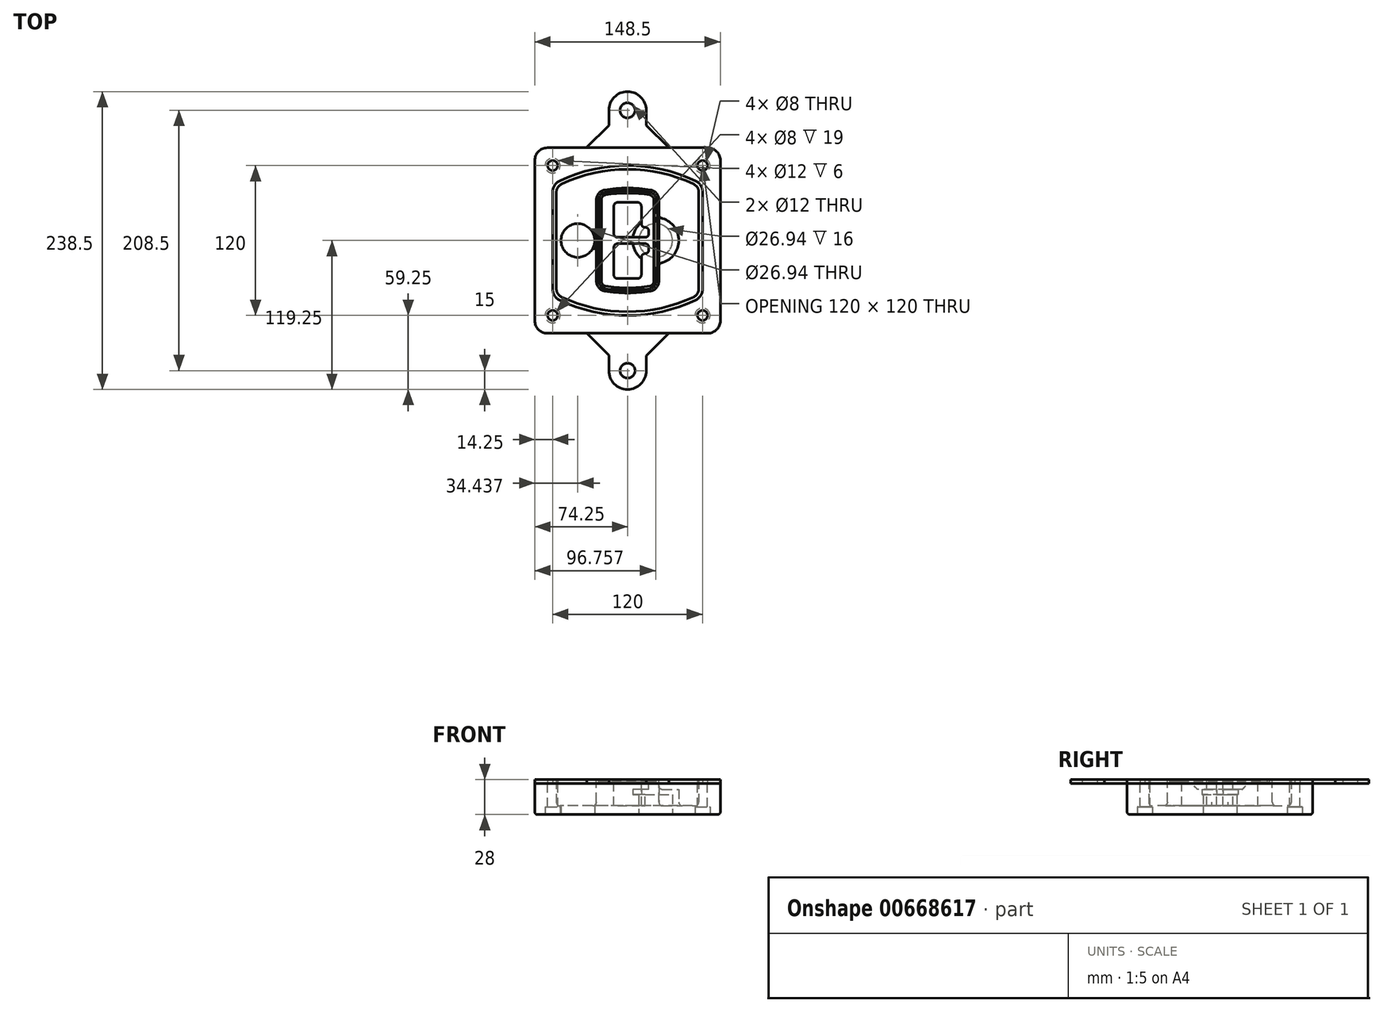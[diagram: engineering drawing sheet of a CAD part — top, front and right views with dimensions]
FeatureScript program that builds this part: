
annotation { "Feature Type Name" : "Feature", "Feature Type Description" : "" }
export const myFeature = defineFeature(function(context is Context, id is Id, definition is map)
    precondition{}
    {
        {
            var Q0;
            Q0=qCreatedBy(makeId("Top.planeOp"),FACE);
            var sketch = newSketch(context, id + "F0", { "sketchPlane" : qUnion([Q0])});
            skPoint(sketch, "E0.rect.middle", {"position": v(0, 0) * mm});
            skLineSegment(sketch, "E1.bottom", {"start": v(-64.25, -74.25) * mm, "end": v(64.25, -74.25) * mm});
            skLineSegment(sketch, "E1.top", {"start": v(-64.25, 74.25) * mm, "end": v(64.25, 74.25) * mm});
            skLineSegment(sketch, "E1.left", {"start": v(-74.25, -64.25) * mm, "end": v(-74.25, 64.25) * mm});
            skLineSegment(sketch, "E1.right", {"start": v(74.25, -64.25) * mm, "end": v(74.25, 64.25) * mm});
            skLineSegment(sketch, "E2", {"start": v(-74.25, 74.25) * mm, "end": v(74.25, -74.25) * mm, "construction": true});
            skLineSegment(sketch, "E3", {"start": v(74.25, 74.25) * mm, "end": v(-74.25, -74.25) * mm, "construction": true});
            skCircle(sketch, "E4", {"center": v(-60, 60) * mm, "radius": 4 * mm});
            skCircle(sketch, "E5", {"center": v(60, 60) * mm, "radius": 4 * mm});
            skCircle(sketch, "E6", {"center": v(60, -60) * mm, "radius": 4 * mm});
            skCircle(sketch, "E7", {"center": v(-60, -60) * mm, "radius": 4 * mm});
            skLineSegment(sketch, "E8", {"start": v(-60, 60) * mm, "end": v(60, 60) * mm, "construction": true});
            skLineSegment(sketch, "E9", {"start": v(60, 60) * mm, "end": v(60, -60) * mm, "construction": true});
            skLineSegment(sketch, "E10", {"start": v(60, -60) * mm, "end": v(-60, -60) * mm, "construction": true});
            skLineSegment(sketch, "E11", {"start": v(-60, -60) * mm, "end": v(-60, 60) * mm, "construction": true});
            skLineSegment(sketch, "E12", {"start": v(-60, 38.83) * mm, "end": v(-60, -38.83) * mm});
            skLineSegment(sketch, "E13", {"start": v(60, 38.83) * mm, "end": v(60, -38.83) * mm});
            skArc(sketch, "E14", {"start": v(54.26, 47.88) * mm, "mid": v(0, 60) * mm, "end": v(-54.26, 47.88) * mm});
            skArc(sketch, "E15", {"start": v(-54.26, -47.88) * mm, "mid": v(0, -60) * mm, "end": v(54.26, -47.88) * mm});
            skLineSegment(sketch, "E16", {"start": v(-60, 0) * mm, "end": v(60, 0) * mm, "construction": true});
            skPoint(sketch, "E17.visualSharp", {"position": v(-60, -45) * mm});
            skArc(sketch, "E17.filletArc", {"start": v(-60, -38.83) * mm, "mid": v(-58.44, -44.2) * mm, "end": v(-54.26, -47.88) * mm});
            skPoint(sketch, "E18.visualSharp", {"position": v(-60, 45) * mm});
            skArc(sketch, "E18.filletArc", {"start": v(-54.26, 47.88) * mm, "mid": v(-58.44, 44.2) * mm, "end": v(-60, 38.83) * mm});
            skPoint(sketch, "E19.visualSharp", {"position": v(60, 45) * mm});
            skArc(sketch, "E19.filletArc", {"start": v(60, 38.83) * mm, "mid": v(58.44, 44.2) * mm, "end": v(54.26, 47.88) * mm});
            skPoint(sketch, "E20.visualSharp", {"position": v(60, -45) * mm});
            skArc(sketch, "E20.filletArc", {"start": v(54.26, -47.88) * mm, "mid": v(58.44, -44.2) * mm, "end": v(60, -38.83) * mm});
            skPoint(sketch, "E21.visualSharp", {"position": v(-74.25, 74.25) * mm});
            skArc(sketch, "E21.filletArc", {"start": v(-64.25, 74.25) * mm, "mid": v(-71.32, 71.32) * mm, "end": v(-74.25, 64.25) * mm});
            skPoint(sketch, "E22.visualSharp", {"position": v(74.25, 74.25) * mm});
            skArc(sketch, "E22.filletArc", {"start": v(74.25, 64.25) * mm, "mid": v(71.32, 71.32) * mm, "end": v(64.25, 74.25) * mm});
            skPoint(sketch, "E23.visualSharp", {"position": v(74.25, -74.25) * mm});
            skArc(sketch, "E23.filletArc", {"start": v(64.25, -74.25) * mm, "mid": v(71.32, -71.32) * mm, "end": v(74.25, -64.25) * mm});
            skPoint(sketch, "E24.visualSharp", {"position": v(-74.25, -74.25) * mm});
            skArc(sketch, "E24.filletArc", {"start": v(-74.25, -64.25) * mm, "mid": v(-71.32, -71.32) * mm, "end": v(-64.25, -74.25) * mm});
            skArc(sketch, "E25.0", {"start": v(57, 38.83) * mm, "mid": v(55.9, 42.58) * mm, "end": v(52.98, 45.17) * mm});
            skLineSegment(sketch, "E25.1", {"start": v(57, 38.83) * mm, "end": v(57, -38.83) * mm});
            skArc(sketch, "E25.2", {"start": v(52.98, -45.17) * mm, "mid": v(55.9, -42.58) * mm, "end": v(57, -38.83) * mm});
            skArc(sketch, "E25.3", {"start": v(-52.98, -45.17) * mm, "mid": v(0, -57) * mm, "end": v(52.98, -45.17) * mm});
            skArc(sketch, "E25.4", {"start": v(-57, -38.83) * mm, "mid": v(-55.9, -42.58) * mm, "end": v(-52.98, -45.17) * mm});
            skArc(sketch, "E25.5", {"start": v(52.98, 45.17) * mm, "mid": v(0, 57) * mm, "end": v(-52.98, 45.17) * mm});
            skLineSegment(sketch, "E25.6", {"start": v(-57, 38.83) * mm, "end": v(-57, -38.83) * mm});
            skArc(sketch, "E25.7", {"start": v(-52.98, 45.17) * mm, "mid": v(-55.9, 42.58) * mm, "end": v(-57, 38.83) * mm});
            skArc(sketch, "E26.0", {"start": v(-55.96, 51.5) * mm, "mid": v(-61.82, 46.33) * mm, "end": v(-64, 38.83) * mm});
            skArc(sketch, "E26.1", {"start": v(55.96, 51.5) * mm, "mid": v(0, 64) * mm, "end": v(-55.96, 51.5) * mm});
            skArc(sketch, "E26.2", {"start": v(64, 38.83) * mm, "mid": v(61.82, 46.33) * mm, "end": v(55.96, 51.5) * mm});
            skLineSegment(sketch, "E26.3", {"start": v(64, 38.83) * mm, "end": v(64, -38.83) * mm});
            skArc(sketch, "E26.4", {"start": v(55.96, -51.5) * mm, "mid": v(61.82, -46.33) * mm, "end": v(64, -38.83) * mm});
            skLineSegment(sketch, "E26.5", {"start": v(-64, 38.83) * mm, "end": v(-64, -38.83) * mm});
            skArc(sketch, "E26.6", {"start": v(-55.96, -51.5) * mm, "mid": v(0, -64) * mm, "end": v(55.96, -51.5) * mm});
            skArc(sketch, "E26.7", {"start": v(-64, -38.83) * mm, "mid": v(-61.82, -46.33) * mm, "end": v(-55.96, -51.5) * mm});
            skSolve(sketch);
        }
        {
            var Q0;
            Q0=makeQuery(id+"F0.imprint","IMPRINT",FACE,{"disambiguationData":[TD([[makeQuery(id+"F0.imprint","IMPRINT",EDGE,{"derivedFrom":sQuery(id+"F0.wireOp",EDGE,"E1.bottom")}),1.0]])]});
            var Q1;
            Q1=makeQuery(id+"F0.imprint","IMPRINT",FACE,{"disambiguationData":[TD([[makeQuery(id+"F0.imprint","IMPRINT",EDGE,{"derivedFrom":sQuery(id+"F0.wireOp",EDGE,"E12")}),1.0]])]});
            var Q2;
            Q2=makeQuery(id+"F0.imprint","IMPRINT",FACE,{"disambiguationData":[TD([[makeQuery(id+"F0.imprint","IMPRINT",EDGE,{"derivedFrom":sQuery(id+"F0.wireOp",EDGE,"E25.0")}),1.0]])]});
            var Q3;
            Q3=makeQuery(id+"F0.imprint","IMPRINT",FACE,{"disambiguationData":[TD([[makeQuery(id+"F0.imprint","IMPRINT",EDGE,{"derivedFrom":sQuery(id+"F0.wireOp",EDGE,"E12")}),-1.0]])]});
            extrude(context, id + "F1", {"entities" : qUnion([Q0, Q1, Q2, Q3]), "oppositeDirection" : true, "depth" : 25 * mm});
        }
        {
            var Q0;
            Q0=makeQuery(id+"F0.imprint","IMPRINT",FACE,{"disambiguationData":[TD([[makeQuery(id+"F0.imprint","IMPRINT",EDGE,{"derivedFrom":sQuery(id+"F0.wireOp",EDGE,"E12")}),1.0]])]});
            extrude(context, id + "F2", {"entities" : qUnion([Q0]), "operationType" : NewBodyOperationType.ADD, "depth" : 3 * mm});
        }
        {
            var Q0;
            Q0=makeQuery(id+"F0.imprint","IMPRINT",FACE,{"disambiguationData":[TD([[makeQuery(id+"F0.imprint","IMPRINT",EDGE,{"derivedFrom":sQuery(id+"F0.wireOp",EDGE,"E25.0")}),1.0]])]});
            extrude(context, id + "F3", {"entities" : qUnion([Q0]), "operationType" : NewBodyOperationType.REMOVE, "oppositeDirection" : true, "depth" : 18 * mm});
        }
        {
            var Q0;
            Q0=makeQuery(id+"F2.opExtrude","CAP_FACE",FACE,{"disambiguationData":[OSD([sQuery(id+"F0.wireOp",EDGE,"E12"),sQuery(id+"F0.wireOp",EDGE,"E13"),sQuery(id+"F0.wireOp",EDGE,"E14"),sQuery(id+"F0.wireOp",EDGE,"E15"),sQuery(id+"F0.wireOp",EDGE,"E17.filletArc"),sQuery(id+"F0.wireOp",EDGE,"E18.filletArc"),sQuery(id+"F0.wireOp",EDGE,"E19.filletArc"),sQuery(id+"F0.wireOp",EDGE,"E20.filletArc"),sQuery(id+"F0.wireOp",EDGE,"E25.0"),sQuery(id+"F0.wireOp",EDGE,"E25.1"),sQuery(id+"F0.wireOp",EDGE,"E25.2"),sQuery(id+"F0.wireOp",EDGE,"E25.3"),sQuery(id+"F0.wireOp",EDGE,"E25.4"),sQuery(id+"F0.wireOp",EDGE,"E25.5"),sQuery(id+"F0.wireOp",EDGE,"E25.6"),sQuery(id+"F0.wireOp",EDGE,"E25.7")])],"isStart":false});
            var sketch = newSketch(context, id + "F4", { "sketchPlane" : qUnion([Q0])});
            skArc(sketch, "E27.0", {"start": v(-18.34, -40.45) * mm, "mid": v(0, -42) * mm, "end": v(18.34, -40.45) * mm});
            skArc(sketch, "E28.0", {"start": v(18.34, 40.45) * mm, "mid": v(0, 42) * mm, "end": v(-18.34, 40.45) * mm});
            skLineSegment(sketch, "E29", {"start": v(-25, 32.57) * mm, "end": v(-25, -32.57) * mm});
            skLineSegment(sketch, "E30", {"start": v(25, 32.57) * mm, "end": v(25, -32.57) * mm});
            skLineSegment(sketch, "E31", {"start": v(-25, 39.1) * mm, "end": v(25, 39.1) * mm, "construction": true});
            skLineSegment(sketch, "E32", {"start": v(-25, -39.1) * mm, "end": v(25, -39.1) * mm, "construction": true});
            skPoint(sketch, "E33.visualSharp", {"position": v(-25, 39.1) * mm});
            skArc(sketch, "E33.filletArc", {"start": v(-18.34, 40.45) * mm, "mid": v(-23.11, 37.73) * mm, "end": v(-25, 32.57) * mm});
            skPoint(sketch, "E34.visualSharp", {"position": v(25, 39.1) * mm});
            skArc(sketch, "E34.filletArc", {"start": v(25, 32.57) * mm, "mid": v(23.11, 37.73) * mm, "end": v(18.34, 40.45) * mm});
            skPoint(sketch, "E35.visualSharp", {"position": v(25, -39.1) * mm});
            skArc(sketch, "E35.filletArc", {"start": v(18.34, -40.45) * mm, "mid": v(23.11, -37.73) * mm, "end": v(25, -32.57) * mm});
            skPoint(sketch, "E36.visualSharp", {"position": v(-25, -39.1) * mm});
            skArc(sketch, "E36.filletArc", {"start": v(-25, -32.57) * mm, "mid": v(-23.11, -37.73) * mm, "end": v(-18.34, -40.45) * mm});
            skArc(sketch, "E37.0", {"start": v(52.98, 45.17) * mm, "mid": v(0, 57) * mm, "end": v(-52.98, 45.17) * mm});
            skArc(sketch, "E37.1", {"start": v(-52.98, 45.17) * mm, "mid": v(-55.9, 42.58) * mm, "end": v(-57, 38.83) * mm});
            skLineSegment(sketch, "E37.2", {"start": v(-57, 38.83) * mm, "end": v(-57, -38.83) * mm});
            skArc(sketch, "E37.3", {"start": v(-57, -38.83) * mm, "mid": v(-55.9, -42.58) * mm, "end": v(-52.98, -45.17) * mm});
            skArc(sketch, "E37.4", {"start": v(-52.98, -45.17) * mm, "mid": v(0, -57) * mm, "end": v(52.98, -45.17) * mm});
            skArc(sketch, "E37.5", {"start": v(52.98, -45.17) * mm, "mid": v(55.9, -42.58) * mm, "end": v(57, -38.83) * mm});
            skLineSegment(sketch, "E37.6", {"start": v(57, 38.83) * mm, "end": v(57, -38.83) * mm});
            skArc(sketch, "E37.7", {"start": v(57, 38.83) * mm, "mid": v(55.9, 42.58) * mm, "end": v(52.98, 45.17) * mm});
            skLineSegment(sketch, "E38.0", {"start": v(23, 32.57) * mm, "end": v(23, -32.57) * mm});
            skArc(sketch, "E38.1", {"start": v(18, -38.48) * mm, "mid": v(21.58, -36.44) * mm, "end": v(23, -32.57) * mm});
            skArc(sketch, "E38.2", {"start": v(-18, -38.48) * mm, "mid": v(0, -40) * mm, "end": v(18, -38.48) * mm});
            skArc(sketch, "E38.3", {"start": v(-23, -32.57) * mm, "mid": v(-21.58, -36.44) * mm, "end": v(-18, -38.48) * mm});
            skLineSegment(sketch, "E38.4", {"start": v(-23, 32.57) * mm, "end": v(-23, -32.57) * mm});
            skArc(sketch, "E38.5", {"start": v(23, 32.57) * mm, "mid": v(21.58, 36.44) * mm, "end": v(18, 38.48) * mm});
            skArc(sketch, "E38.6", {"start": v(-18, 38.48) * mm, "mid": v(-21.58, 36.44) * mm, "end": v(-23, 32.57) * mm});
            skArc(sketch, "E38.7", {"start": v(18, 38.48) * mm, "mid": v(0, 40) * mm, "end": v(-18, 38.48) * mm});
            skArc(sketch, "E39.0", {"start": v(21, 32.57) * mm, "mid": v(20.06, 35.15) * mm, "end": v(17.67, 36.5) * mm});
            skLineSegment(sketch, "E39.1", {"start": v(21, 32.57) * mm, "end": v(21, -32.57) * mm});
            skArc(sketch, "E39.2", {"start": v(17.67, -36.5) * mm, "mid": v(20.06, -35.15) * mm, "end": v(21, -32.57) * mm});
            skArc(sketch, "E39.3", {"start": v(-17.67, -36.5) * mm, "mid": v(0, -38) * mm, "end": v(17.67, -36.5) * mm});
            skArc(sketch, "E39.4", {"start": v(-21, -32.57) * mm, "mid": v(-20.06, -35.15) * mm, "end": v(-17.67, -36.5) * mm});
            skArc(sketch, "E39.5", {"start": v(17.67, 36.5) * mm, "mid": v(0, 38) * mm, "end": v(-17.67, 36.5) * mm});
            skLineSegment(sketch, "E39.6", {"start": v(-21, 32.57) * mm, "end": v(-21, -32.57) * mm});
            skArc(sketch, "E39.7", {"start": v(-17.67, 36.5) * mm, "mid": v(-20.06, 35.15) * mm, "end": v(-21, 32.57) * mm});
            skLineSegment(sketch, "E40", {"start": v(-25, 0) * mm, "end": v(25, 0) * mm, "construction": true});
            skLineSegment(sketch, "E41", {"start": v(-11, 5.5) * mm, "end": v(-11, 27.5) * mm});
            skLineSegment(sketch, "E42", {"start": v(-8, 30.5) * mm, "end": v(8, 30.5) * mm});
            skLineSegment(sketch, "E43", {"start": v(11, 27.5) * mm, "end": v(11, 13.5) * mm});
            skLineSegment(sketch, "E44", {"start": v(14, 10.5) * mm, "end": v(14, 10.5) * mm});
            skLineSegment(sketch, "E45", {"start": v(17, 7.5) * mm, "end": v(17, 5.5) * mm});
            skLineSegment(sketch, "E46", {"start": v(14, 2.5) * mm, "end": v(-8, 2.5) * mm});
            skPoint(sketch, "E47.visualSharp", {"position": v(-11, 30.5) * mm});
            skArc(sketch, "E47.filletArc", {"start": v(-8, 30.5) * mm, "mid": v(-10.12, 29.62) * mm, "end": v(-11, 27.5) * mm});
            skPoint(sketch, "E48.visualSharp", {"position": v(11, 30.5) * mm});
            skArc(sketch, "E48.filletArc", {"start": v(11, 27.5) * mm, "mid": v(10.12, 29.62) * mm, "end": v(8, 30.5) * mm});
            skPoint(sketch, "E49.visualSharp", {"position": v(11, 10.5) * mm});
            skArc(sketch, "E49.filletArc", {"start": v(11, 13.5) * mm, "mid": v(11.88, 11.38) * mm, "end": v(14, 10.5) * mm});
            skPoint(sketch, "E50.visualSharp", {"position": v(17, 10.5) * mm});
            skArc(sketch, "E50.filletArc", {"start": v(17, 7.5) * mm, "mid": v(16.12, 9.62) * mm, "end": v(14, 10.5) * mm});
            skPoint(sketch, "E51.visualSharp", {"position": v(17, 2.5) * mm});
            skArc(sketch, "E51.filletArc", {"start": v(14, 2.5) * mm, "mid": v(16.12, 3.38) * mm, "end": v(17, 5.5) * mm});
            skPoint(sketch, "E52.visualSharp", {"position": v(-11, 2.5) * mm});
            skArc(sketch, "E52.filletArc", {"start": v(-11, 5.5) * mm, "mid": v(-10.12, 3.38) * mm, "end": v(-8, 2.5) * mm});
            skLineSegment(sketch, "E53.0.MirrorCS", {"start": v(14, -2.5) * mm, "end": v(-8, -2.5) * mm});
            skArc(sketch, "E54.0.MirrorCS", {"start": v(-11, -5.5) * mm, "mid": v(-10.12, -3.38) * mm, "end": v(-8, -2.5) * mm});
            skLineSegment(sketch, "E55.0.MirrorCS", {"start": v(-11, -5.5) * mm, "end": v(-11, -27.5) * mm});
            skArc(sketch, "E56.0.MirrorCS", {"start": v(-8, -30.5) * mm, "mid": v(-10.12, -29.62) * mm, "end": v(-11, -27.5) * mm});
            skLineSegment(sketch, "E57.0.MirrorCS", {"start": v(-8, -30.5) * mm, "end": v(8, -30.5) * mm});
            skArc(sketch, "E58.0.MirrorCS", {"start": v(11, -27.5) * mm, "mid": v(10.12, -29.62) * mm, "end": v(8, -30.5) * mm});
            skLineSegment(sketch, "E59.0.MirrorCS", {"start": v(11, -27.5) * mm, "end": v(11, -13.5) * mm});
            skArc(sketch, "E60.0.MirrorCS", {"start": v(11, -13.5) * mm, "mid": v(11.88, -11.38) * mm, "end": v(14, -10.5) * mm});
            skArc(sketch, "E61.0.MirrorCS", {"start": v(17, -7.5) * mm, "mid": v(16.12, -9.62) * mm, "end": v(14, -10.5) * mm});
            skLineSegment(sketch, "E62.0.MirrorCS", {"start": v(17, -7.5) * mm, "end": v(17, -5.5) * mm});
            skArc(sketch, "E63.0.MirrorCS", {"start": v(14, -2.5) * mm, "mid": v(16.12, -3.38) * mm, "end": v(17, -5.5) * mm});
            skSolve(sketch);
        }
        {
            var Q0;
            Q0=makeQuery(id+"F4.imprint","IMPRINT",FACE,{"disambiguationData":[TD([[makeQuery(id+"F4.imprint","IMPRINT",EDGE,{"derivedFrom":sQuery(id+"F4.wireOp",EDGE,"E27.0")}),1.0]])]});
            var Q1;
            Q1=makeQuery(id+"F4.imprint","IMPRINT",FACE,{"disambiguationData":[TD([[makeQuery(id+"F4.imprint","IMPRINT",EDGE,{"derivedFrom":sQuery(id+"F4.wireOp",EDGE,"E38.0")}),-1.0]])]});
            var Q2;
            Q2=makeQuery(id+"F4.imprint","IMPRINT",FACE,{"disambiguationData":[TD([[makeQuery(id+"F4.imprint","IMPRINT",EDGE,{"derivedFrom":sQuery(id+"F4.wireOp",EDGE,"E39.0")}),1.0]])]});
            extrude(context, id + "F5", {"entities" : qUnion([Q0, Q1, Q2]), "operationType" : NewBodyOperationType.ADD, "endBound" : BoundingType.UP_TO_NEXT, "oppositeDirection" : true, "depth" : 25 * mm});
        }
        {
            var Q0;
            Q0=makeQuery(id+"F4.imprint","IMPRINT",FACE,{"disambiguationData":[TD([[makeQuery(id+"F4.imprint","IMPRINT",EDGE,{"derivedFrom":sQuery(id+"F4.wireOp",EDGE,"E38.0")}),-1.0]])]});
            extrude(context, id + "F6", {"entities" : qUnion([Q0]), "operationType" : NewBodyOperationType.REMOVE, "oppositeDirection" : true, "depth" : 2 * mm});
        }
        {
            var Q0;
            Q0=makeQuery(id+"F1.opExtrude","CAP_FACE",FACE,{"disambiguationData":[OSD([sQuery(id+"F0.wireOp",EDGE,"E1.bottom"),sQuery(id+"F0.wireOp",EDGE,"E1.top"),sQuery(id+"F0.wireOp",EDGE,"E1.left"),sQuery(id+"F0.wireOp",EDGE,"E1.right"),sQuery(id+"F0.wireOp",EDGE,"E4"),sQuery(id+"F0.wireOp",EDGE,"E5"),sQuery(id+"F0.wireOp",EDGE,"E6"),sQuery(id+"F0.wireOp",EDGE,"E7"),sQuery(id+"F0.wireOp",EDGE,"E21.filletArc"),sQuery(id+"F0.wireOp",EDGE,"E22.filletArc"),sQuery(id+"F0.wireOp",EDGE,"E23.filletArc"),sQuery(id+"F0.wireOp",EDGE,"E24.filletArc")])],"isStart":false});
            var sketch = newSketch(context, id + "F7", { "sketchPlane" : qUnion([Q0])});
            skCircle(sketch, "E64", {"center": v(22.5, 0) * mm, "radius": 13.47 * mm});
            skCircle(sketch, "E65", {"center": v(-39.81, 0) * mm, "radius": 13.47 * mm});
            skLineSegment(sketch, "E66", {"start": v(74.25, 0) * mm, "end": v(-74.25, 0) * mm});
            skCircle(sketch, "E67", {"center": v(22.5, 0) * mm, "radius": 18.47 * mm});
            skCircle(sketch, "E68", {"center": v(60, -60) * mm, "radius": 6 * mm});
            skCircle(sketch, "E69", {"center": v(-60, -60) * mm, "radius": 6 * mm});
            skCircle(sketch, "E70", {"center": v(-60, 60) * mm, "radius": 6 * mm});
            skCircle(sketch, "E71", {"center": v(60, 60) * mm, "radius": 6 * mm});
            skSolve(sketch);
        }
        {
            var Q0;
            {var subQ1=sQuery(id+"F7.wireOp",EDGE,"E66");var subQ4=sQuery(id+"F7.wireOp",EDGE,"E64");var subQ6=makeQuery(id+"F7.imprint","INTERSECT",VERTEX,{"disambiguationData":[OD(0.0)],"derivedFrom":[subQ4,subQ1]});Q0=makeQuery(id+"F7.imprint","IMPRINT",FACE,{"disambiguationData":[TD([[makeQuery(id+"F7.imprint","IMPRINT",EDGE,{"disambiguationData":[TD([[subQ6,-1.0]])],"derivedFrom":subQ4}),-1.0]])]});}
            var Q1;
            {var subQ0=sQuery(id+"F7.wireOp",EDGE,"E66");var subQ1=sQuery(id+"F7.wireOp",EDGE,"E64");var subQ3=makeQuery(id+"F7.imprint","INTERSECT",VERTEX,{"disambiguationData":[OD(0.0)],"derivedFrom":[subQ1,subQ0]});Q1=makeQuery(id+"F7.imprint","IMPRINT",FACE,{"disambiguationData":[TD([[makeQuery(id+"F7.imprint","IMPRINT",EDGE,{"disambiguationData":[TD([[subQ3,-1.0]])],"derivedFrom":subQ1}),1.0]])]});}
            var Q2;
            {var subQ0=sQuery(id+"F7.wireOp",EDGE,"E66");var subQ1=sQuery(id+"F7.wireOp",EDGE,"E64");var subQ3=makeQuery(id+"F7.imprint","INTERSECT",VERTEX,{"disambiguationData":[OD(0.0)],"derivedFrom":[subQ1,subQ0]});Q2=makeQuery(id+"F7.imprint","IMPRINT",FACE,{"disambiguationData":[TD([[makeQuery(id+"F7.imprint","IMPRINT",EDGE,{"disambiguationData":[TD([[subQ3,1.0]])],"derivedFrom":subQ1}),1.0]])]});}
            var Q3;
            {var subQ1=sQuery(id+"F7.wireOp",EDGE,"E66");var subQ4=sQuery(id+"F7.wireOp",EDGE,"E64");var subQ6=makeQuery(id+"F7.imprint","INTERSECT",VERTEX,{"disambiguationData":[OD(0.0)],"derivedFrom":[subQ4,subQ1]});Q3=makeQuery(id+"F7.imprint","IMPRINT",FACE,{"disambiguationData":[TD([[makeQuery(id+"F7.imprint","IMPRINT",EDGE,{"disambiguationData":[TD([[subQ6,1.0]])],"derivedFrom":subQ4}),-1.0]])]});}
            extrude(context, id + "F8", {"entities" : qUnion([Q0, Q1, Q2, Q3]), "operationType" : NewBodyOperationType.ADD, "oppositeDirection" : true, "depth" : 20 * mm});
        }
        {
            var Q0;
            {var subQ0=sQuery(id+"F7.wireOp",EDGE,"E66");var subQ1=sQuery(id+"F7.wireOp",EDGE,"E64");var subQ3=makeQuery(id+"F7.imprint","INTERSECT",VERTEX,{"disambiguationData":[OD(0.0)],"derivedFrom":[subQ1,subQ0]});Q0=makeQuery(id+"F7.imprint","IMPRINT",FACE,{"disambiguationData":[TD([[makeQuery(id+"F7.imprint","IMPRINT",EDGE,{"disambiguationData":[TD([[subQ3,-1.0]])],"derivedFrom":subQ1}),1.0]])]});}
            var Q1;
            {var subQ0=sQuery(id+"F7.wireOp",EDGE,"E66");var subQ1=sQuery(id+"F7.wireOp",EDGE,"E64");var subQ3=makeQuery(id+"F7.imprint","INTERSECT",VERTEX,{"disambiguationData":[OD(0.0)],"derivedFrom":[subQ1,subQ0]});Q1=makeQuery(id+"F7.imprint","IMPRINT",FACE,{"disambiguationData":[TD([[makeQuery(id+"F7.imprint","IMPRINT",EDGE,{"disambiguationData":[TD([[subQ3,1.0]])],"derivedFrom":subQ1}),1.0]])]});}
            extrude(context, id + "F9", {"entities" : qUnion([Q0, Q1]), "operationType" : NewBodyOperationType.REMOVE, "oppositeDirection" : true, "depth" : 16 * mm});
        }
        {
            var Q0;
            {var subQ0=sQuery(id+"F7.wireOp",EDGE,"E66");var subQ1=sQuery(id+"F7.wireOp",EDGE,"E65");var subQ3=makeQuery(id+"F7.imprint","INTERSECT",VERTEX,{"disambiguationData":[OD(0.0)],"derivedFrom":[subQ1,subQ0]});Q0=makeQuery(id+"F7.imprint","IMPRINT",FACE,{"disambiguationData":[TD([[makeQuery(id+"F7.imprint","IMPRINT",EDGE,{"disambiguationData":[TD([[subQ3,-1.0]])],"derivedFrom":subQ1}),1.0]])]});}
            var Q1;
            {var subQ0=sQuery(id+"F7.wireOp",EDGE,"E66");var subQ1=sQuery(id+"F7.wireOp",EDGE,"E65");var subQ3=makeQuery(id+"F7.imprint","INTERSECT",VERTEX,{"disambiguationData":[OD(0.0)],"derivedFrom":[subQ1,subQ0]});Q1=makeQuery(id+"F7.imprint","IMPRINT",FACE,{"disambiguationData":[TD([[makeQuery(id+"F7.imprint","IMPRINT",EDGE,{"disambiguationData":[TD([[subQ3,1.0]])],"derivedFrom":subQ1}),1.0]])]});}
            extrude(context, id + "F10", {"entities" : qUnion([Q0, Q1]), "operationType" : NewBodyOperationType.REMOVE, "oppositeDirection" : true, "depth" : 25 * mm});
        }
        {
            var Q0;
            Q0=makeQuery(id+"F7.imprint","IMPRINT",FACE,{"disambiguationData":[TD([[makeQuery(id+"F7.imprint","IMPRINT",EDGE,{"derivedFrom":sQuery(id+"F7.wireOp",EDGE,"E68")}),1.0]])]});
            var Q1;
            Q1=makeQuery(id+"F7.imprint","IMPRINT",FACE,{"disambiguationData":[TD([[makeQuery(id+"F7.imprint","IMPRINT",EDGE,{"derivedFrom":makeQuery(id+"F1.opExtrude","CAP_EDGE",EDGE,{"disambiguationData":[OSD([sQuery(id+"F0.wireOp",EDGE,"E5")])],"isStart":false})}),-1.0]])]});
            var Q2;
            Q2=makeQuery(id+"F7.imprint","IMPRINT",FACE,{"disambiguationData":[TD([[makeQuery(id+"F7.imprint","IMPRINT",EDGE,{"derivedFrom":sQuery(id+"F7.wireOp",EDGE,"E69")}),1.0]])]});
            var Q3;
            Q3=makeQuery(id+"F7.imprint","IMPRINT",FACE,{"disambiguationData":[TD([[makeQuery(id+"F7.imprint","IMPRINT",EDGE,{"derivedFrom":makeQuery(id+"F1.opExtrude","CAP_EDGE",EDGE,{"disambiguationData":[OSD([sQuery(id+"F0.wireOp",EDGE,"E4")])],"isStart":false})}),-1.0]])]});
            var Q4;
            Q4=makeQuery(id+"F7.imprint","IMPRINT",FACE,{"disambiguationData":[TD([[makeQuery(id+"F7.imprint","IMPRINT",EDGE,{"derivedFrom":sQuery(id+"F7.wireOp",EDGE,"E70")}),1.0]])]});
            var Q5;
            Q5=makeQuery(id+"F7.imprint","IMPRINT",FACE,{"disambiguationData":[TD([[makeQuery(id+"F7.imprint","IMPRINT",EDGE,{"derivedFrom":makeQuery(id+"F1.opExtrude","CAP_EDGE",EDGE,{"disambiguationData":[OSD([sQuery(id+"F0.wireOp",EDGE,"E7")])],"isStart":false})}),-1.0]])]});
            var Q6;
            Q6=makeQuery(id+"F7.imprint","IMPRINT",FACE,{"disambiguationData":[TD([[makeQuery(id+"F7.imprint","IMPRINT",EDGE,{"derivedFrom":sQuery(id+"F7.wireOp",EDGE,"E71")}),1.0]])]});
            var Q7;
            Q7=makeQuery(id+"F7.imprint","IMPRINT",FACE,{"disambiguationData":[TD([[makeQuery(id+"F7.imprint","IMPRINT",EDGE,{"derivedFrom":makeQuery(id+"F1.opExtrude","CAP_EDGE",EDGE,{"disambiguationData":[OSD([sQuery(id+"F0.wireOp",EDGE,"E6")])],"isStart":false})}),-1.0]])]});
            extrude(context, id + "F11", {"entities" : qUnion([Q0, Q1, Q2, Q3, Q4, Q5, Q6, Q7]), "operationType" : NewBodyOperationType.REMOVE, "oppositeDirection" : true, "depth" : 6 * mm});
        }
        {
            var Q0;
            Q0=makeQuery(id+"F9.boolean.opBoolean","COPY",FACE,{"derivedFrom":makeQuery(id+"F9.opExtrude","CAP_FACE",FACE,{"disambiguationData":[OSD([sQuery(id+"F7.wireOp",EDGE,"E64")])],"isStart":false})});
            var sketch = newSketch(context, id + "F12", { "sketchPlane" : qUnion([Q0])});
            skArc(sketch, "E72.0", {"start": v(11, 14.45) * mm, "mid": v(6.45, 9.13) * mm, "end": v(4.2, 2.5) * mm});
            skArc(sketch, "E72.1", {"start": v(4.2, -2.5) * mm, "mid": v(6.45, -9.13) * mm, "end": v(11, -14.45) * mm});
            skLineSegment(sketch, "E73", {"start": v(4.2, -2.5) * mm, "end": v(14, -2.5) * mm});
            skLineSegment(sketch, "E74.0", {"start": v(14, 2.5) * mm, "end": v(4.2, 2.5) * mm});
            skArc(sketch, "E74.1", {"start": v(14, 2.5) * mm, "mid": v(16.12, 3.38) * mm, "end": v(17, 5.5) * mm});
            skLineSegment(sketch, "E74.2", {"start": v(17, 7.5) * mm, "end": v(17, 5.5) * mm});
            skArc(sketch, "E74.3", {"start": v(17, 7.5) * mm, "mid": v(16.12, 9.62) * mm, "end": v(14, 10.5) * mm});
            skArc(sketch, "E74.4", {"start": v(11, 13.5) * mm, "mid": v(11.88, 11.38) * mm, "end": v(14, 10.5) * mm});
            skLineSegment(sketch, "E74.5", {"start": v(11, 14.45) * mm, "end": v(11, 13.5) * mm});
            skLineSegment(sketch, "E74.7", {"start": v(14, -2.5) * mm, "end": v(4.2, -2.5) * mm});
            skArc(sketch, "E74.8", {"start": v(14, -2.5) * mm, "mid": v(16.12, -3.38) * mm, "end": v(17, -5.5) * mm});
            skLineSegment(sketch, "E74.9", {"start": v(17, -7.5) * mm, "end": v(17, -5.5) * mm});
            skArc(sketch, "E74.10", {"start": v(17, -7.5) * mm, "mid": v(16.12, -9.62) * mm, "end": v(14, -10.5) * mm});
            skArc(sketch, "E74.11", {"start": v(11, -13.5) * mm, "mid": v(11.88, -11.38) * mm, "end": v(14, -10.5) * mm});
            skLineSegment(sketch, "E74.12", {"start": v(11, -14.45) * mm, "end": v(11, -13.5) * mm});
            skPoint(sketch, "E75.orphan", {"position": v(11, -27.5) * mm});
            skPoint(sketch, "E76.orphan", {"position": v(-8, -2.5) * mm});
            skPoint(sketch, "E77.orphan", {"position": v(-8, 2.5) * mm});
            skPoint(sketch, "E78.orphan", {"position": v(11, 27.5) * mm});
            skSolve(sketch);
        }
        {
            var Q0;
            {var subQ7=sQuery(id+"F12.wireOp",EDGE,"E72.0");var subQ14=sQuery(id+"F12.wireOp",EDGE,"E72.1");var subQ16=sQuery(id+"F12.wireOp",EDGE,"E74.1");var subQ18=sQuery(id+"F12.wireOp",EDGE,"E74.8");Q0=qUnion([makeQuery(id+"F12.imprint","IMPRINT",FACE,{"disambiguationData":[TD([[makeQuery(id+"F12.imprint","IMPRINT",EDGE,{"derivedFrom":subQ7}),1.0]])]}),makeQuery(id+"F12.imprint","IMPRINT",FACE,{"disambiguationData":[TD([[makeQuery(id+"F12.imprint","IMPRINT",EDGE,{"derivedFrom":subQ14}),1.0]])]}),makeQuery(id+"F12.imprint","IMPRINT",FACE,{"disambiguationData":[TD([[makeQuery(id+"F12.imprint","IMPRINT",EDGE,{"derivedFrom":subQ16}),1.0]])]}),makeQuery(id+"F12.imprint","IMPRINT",FACE,{"disambiguationData":[TD([[makeQuery(id+"F12.imprint","IMPRINT",EDGE,{"derivedFrom":subQ18}),-1.0]])]})]);}
            var Q1;
            Q1=makeQuery(id+"F5.boolean.opBoolean","SPLIT",FACE,{"disambiguationData":[TD([makeQuery(id+"F5.opExtrude","SWEPT_FACE",FACE,{"disambiguationData":[OSD([sQuery(id+"F4.wireOp",EDGE,"E41")])]})])],"derivedFrom":makeQuery(id+"F3.boolean.opBoolean","COPY",FACE,{"derivedFrom":makeQuery(id+"F3.opExtrude","CAP_FACE",FACE,{"disambiguationData":[OSD([sQuery(id+"F0.wireOp",EDGE,"E25.0"),sQuery(id+"F0.wireOp",EDGE,"E25.1"),sQuery(id+"F0.wireOp",EDGE,"E25.2"),sQuery(id+"F0.wireOp",EDGE,"E25.3"),sQuery(id+"F0.wireOp",EDGE,"E25.4"),sQuery(id+"F0.wireOp",EDGE,"E25.5"),sQuery(id+"F0.wireOp",EDGE,"E25.6"),sQuery(id+"F0.wireOp",EDGE,"E25.7")])],"isStart":false})})});
            extrude(context, id + "F13", {"entities" : qUnion([Q0]), "operationType" : NewBodyOperationType.REMOVE, "endBound" : BoundingType.UP_TO_SURFACE, "endBoundEntityFace" : qUnion([Q1]), "depth" : 25 * mm});
        }
        {
            var Q0;
            Q0=makeQuery(id+"F3.boolean.opBoolean","COPY",EDGE,{"derivedFrom":makeQuery(id+"F3.opExtrude","CAP_EDGE",EDGE,{"disambiguationData":[OSD([sQuery(id+"F0.wireOp",EDGE,"E25.6")])],"isStart":false})});
            var Q1;
            Q1=makeQuery(id+"F8.boolean.opBoolean","INTERSECT",EDGE,{"derivedFrom":[makeQuery(id+"F5.opExtrude","SWEPT_FACE",FACE,{"disambiguationData":[OSD([sQuery(id+"F4.wireOp",EDGE,"E30")])]}),makeQuery(id+"F8.opExtrude","CAP_FACE",FACE,{"disambiguationData":[OSD([sQuery(id+"F7.wireOp",EDGE,"E67")])],"isStart":false})]});
            var Q2;
            Q2=makeQuery(id+"F8.boolean.opBoolean","INTERSECT",EDGE,{"disambiguationData":[OD(1.0)],"derivedFrom":[makeQuery(id+"F5.opExtrude","SWEPT_FACE",FACE,{"disambiguationData":[OSD([sQuery(id+"F4.wireOp",EDGE,"E30")])]}),makeQuery(id+"F8.opExtrude","SWEPT_FACE",FACE,{"disambiguationData":[OSD([sQuery(id+"F7.wireOp",EDGE,"E67")])]})]});
            var Q3;
            {var subQ0=sQuery(id+"F4.wireOp",EDGE,"E30");Q3=makeQuery(id+"F8.boolean.opBoolean","SPLIT",EDGE,{"disambiguationData":[TD([makeQuery(id+"F5.opExtrude","SWEPT_FACE",FACE,{"disambiguationData":[OSD([sQuery(id+"F4.wireOp",EDGE,"E35.filletArc")])]})])],"derivedFrom":makeQuery(id+"F5.opExtrude","CAP_EDGE",EDGE,{"disambiguationData":[OSD([subQ0])],"isStart":false})});}
            var Q4;
            {var subQ0=sQuery(id+"F0.wireOp",EDGE,"E25.7");var subQ1=sQuery(id+"F0.wireOp",EDGE,"E25.1");var subQ2=sQuery(id+"F0.wireOp",EDGE,"E25.6");var subQ3=sQuery(id+"F0.wireOp",EDGE,"E25.5");var subQ4=sQuery(id+"F0.wireOp",EDGE,"E25.4");var subQ5=sQuery(id+"F0.wireOp",EDGE,"E25.0");var subQ6=sQuery(id+"F0.wireOp",EDGE,"E25.2");var subQ7=sQuery(id+"F0.wireOp",EDGE,"E25.3");Q4=makeQuery(id+"F8.boolean.opBoolean","INTERSECT",EDGE,{"derivedFrom":[makeQuery(id+"F5.boolean.opBoolean","SPLIT",FACE,{"disambiguationData":[TD([makeQuery(id+"F2.opExtrude","SWEPT_FACE",FACE,{"disambiguationData":[OSD([subQ5])]})])],"derivedFrom":makeQuery(id+"F3.boolean.opBoolean","COPY",FACE,{"derivedFrom":makeQuery(id+"F3.opExtrude","CAP_FACE",FACE,{"disambiguationData":[OSD([subQ5,subQ1,subQ6,subQ7,subQ4,subQ3,subQ2,subQ0])],"isStart":false})})}),makeQuery(id+"F8.opExtrude","SWEPT_FACE",FACE,{"disambiguationData":[OSD([sQuery(id+"F7.wireOp",EDGE,"E67")])]})]});}
            var Q5;
            Q5=makeQuery(id+"F8.boolean.opBoolean","INTERSECT",EDGE,{"disambiguationData":[OD(0.0)],"derivedFrom":[makeQuery(id+"F5.opExtrude","SWEPT_FACE",FACE,{"disambiguationData":[OSD([sQuery(id+"F4.wireOp",EDGE,"E30")])]}),makeQuery(id+"F8.opExtrude","SWEPT_FACE",FACE,{"disambiguationData":[OSD([sQuery(id+"F7.wireOp",EDGE,"E67")])]})]});
            fillet(context, id + "F14", {"entities" : qUnion([Q0, Q1, Q2, Q3, Q4, Q5]), "radius" : 3 * mm, "tangentPropagation" : true, "allowEdgeOverflow" : false});
        }
        {
            var Q0;
            Q0=makeQuery(id+"F1.opExtrude","CAP_EDGE",EDGE,{"disambiguationData":[OSD([sQuery(id+"F0.wireOp",EDGE,"E1.bottom")])],"isStart":false});
            fillet(context, id + "F15", {"entities" : qUnion([Q0]), "radius" : 2 * mm, "tangentPropagation" : true, "allowEdgeOverflow" : false});
        }
        {
            var Q0;
            {var subQ0=sQuery(id+"F0.wireOp",EDGE,"E21.filletArc");var subQ1=sQuery(id+"F0.wireOp",EDGE,"E7");var subQ2=sQuery(id+"F0.wireOp",EDGE,"E6");var subQ3=sQuery(id+"F0.wireOp",EDGE,"E5");var subQ4=sQuery(id+"F0.wireOp",EDGE,"E4");var subQ5=sQuery(id+"F0.wireOp",EDGE,"E22.filletArc");var subQ6=sQuery(id+"F0.wireOp",EDGE,"E1.bottom");var subQ7=sQuery(id+"F0.wireOp",EDGE,"E1.right");var subQ8=sQuery(id+"F0.wireOp",EDGE,"E1.top");var subQ9=sQuery(id+"F0.wireOp",EDGE,"E1.left");var subQ10=sQuery(id+"F0.wireOp",EDGE,"E23.filletArc");var subQ11=sQuery(id+"F0.wireOp",EDGE,"E24.filletArc");Q0=makeQuery(id+"F2.boolean.opBoolean","SPLIT",FACE,{"disambiguationData":[TD([makeQuery(id+"F1.opExtrude","SWEPT_FACE",FACE,{"disambiguationData":[OSD([subQ6])]})])],"derivedFrom":makeQuery(id+"F1.opExtrude","CAP_FACE",FACE,{"disambiguationData":[OSD([subQ6,subQ8,subQ9,subQ7,subQ4,subQ3,subQ2,subQ1,subQ0,subQ5,subQ10,subQ11])],"isStart":true})});}
            var sketch = newSketch(context, id + "F16", { "sketchPlane" : qUnion([Q0])});
            skLineSegment(sketch, "E79", {"start": v(0, 74.25) * mm, "end": v(0, 104.25) * mm});
            skCircle(sketch, "E80", {"center": v(0, 104.25) * mm, "radius": 6 * mm});
            skArc(sketch, "E81", {"start": v(15, 104.25) * mm, "mid": v(0, 119.25) * mm, "end": v(-15, 104.25) * mm});
            skLineSegment(sketch, "E82", {"start": v(15, 104.25) * mm, "end": v(15, 92.25) * mm});
            skLineSegment(sketch, "E83", {"start": v(-15, 104.25) * mm, "end": v(-15, 92.25) * mm});
            skLineSegment(sketch, "E84", {"start": v(15, 92.25) * mm, "end": v(33, 74.25) * mm});
            skLineSegment(sketch, "E85", {"start": v(-15, 92.25) * mm, "end": v(-33, 74.25) * mm});
            skLineSegment(sketch, "E86", {"start": v(0, -74.25) * mm, "end": v(0, -104.25) * mm});
            skArc(sketch, "E87", {"start": v(-15, -104.25) * mm, "mid": v(-0.01, -119.25) * mm, "end": v(15, -104.27) * mm});
            skLineSegment(sketch, "E88", {"start": v(15, -104.27) * mm, "end": v(15.02, -92.27) * mm});
            skCircle(sketch, "E89", {"center": v(0, -104.25) * mm, "radius": 6 * mm});
            skLineSegment(sketch, "E90", {"start": v(-15, -104.25) * mm, "end": v(-15, -92.02) * mm});
            skLineSegment(sketch, "E91", {"start": v(-15, -92.02) * mm, "end": v(-32.77, -74.25) * mm});
            skLineSegment(sketch, "E92", {"start": v(15.02, -92.27) * mm, "end": v(33.04, -74.25) * mm});
            skText(sketch, "E93", { "text": "Ivan Sidoriak \n417,707.255 mm^3", "fontName": "NotoSans-Regular.ttf"});
            const initialGuessF16  = {"E93": [0.06015, 0.10067, 1, 0, 0.02004]};
            skSetInitialGuess(sketch, initialGuessF16);
            skSolve(sketch);
        }
        {
            var Q0;
            Q0=makeQuery(id+"F16.imprint","IMPRINT",FACE,{"disambiguationData":[TD([[makeQuery(id+"F16.imprint","IMPRINT",EDGE,{"derivedFrom":sQuery(id+"F16.wireOp",EDGE,"E87")}),1.0]])]});
            var Q1;
            Q1=makeQuery(id+"F16.imprint","IMPRINT",FACE,{"disambiguationData":[TD([[makeQuery(id+"F16.imprint","IMPRINT",EDGE,{"derivedFrom":sQuery(id+"F16.wireOp",EDGE,"E80")}),-1.0]])]});
            var Q2;
            Q2=makeQuery(id+"F2.opExtrude","CAP_FACE",FACE,{"disambiguationData":[OSD([sQuery(id+"F0.wireOp",EDGE,"E12"),sQuery(id+"F0.wireOp",EDGE,"E13"),sQuery(id+"F0.wireOp",EDGE,"E14"),sQuery(id+"F0.wireOp",EDGE,"E15"),sQuery(id+"F0.wireOp",EDGE,"E17.filletArc"),sQuery(id+"F0.wireOp",EDGE,"E18.filletArc"),sQuery(id+"F0.wireOp",EDGE,"E19.filletArc"),sQuery(id+"F0.wireOp",EDGE,"E20.filletArc"),sQuery(id+"F0.wireOp",EDGE,"E25.0"),sQuery(id+"F0.wireOp",EDGE,"E25.1"),sQuery(id+"F0.wireOp",EDGE,"E25.2"),sQuery(id+"F0.wireOp",EDGE,"E25.3"),sQuery(id+"F0.wireOp",EDGE,"E25.4"),sQuery(id+"F0.wireOp",EDGE,"E25.5"),sQuery(id+"F0.wireOp",EDGE,"E25.6"),sQuery(id+"F0.wireOp",EDGE,"E25.7")])],"isStart":false});
            extrude(context, id + "F17", {"entities" : qUnion([Q0, Q1]), "endBound" : BoundingType.UP_TO_SURFACE, "depth" : 25.4 * mm, "endBoundEntityFace" : qUnion([Q2]), "offsetDistance" : 25.4 * mm});
        }
        {
            var Q0;
            {var subQ0=sQuery(id+"F0.wireOp",EDGE,"E21.filletArc");var subQ1=sQuery(id+"F0.wireOp",EDGE,"E7");var subQ2=sQuery(id+"F0.wireOp",EDGE,"E6");var subQ3=sQuery(id+"F0.wireOp",EDGE,"E5");var subQ4=sQuery(id+"F0.wireOp",EDGE,"E4");var subQ5=sQuery(id+"F0.wireOp",EDGE,"E22.filletArc");var subQ6=sQuery(id+"F0.wireOp",EDGE,"E1.bottom");var subQ7=sQuery(id+"F0.wireOp",EDGE,"E1.right");var subQ8=sQuery(id+"F0.wireOp",EDGE,"E1.top");var subQ9=sQuery(id+"F0.wireOp",EDGE,"E1.left");var subQ10=sQuery(id+"F0.wireOp",EDGE,"E23.filletArc");var subQ11=sQuery(id+"F0.wireOp",EDGE,"E24.filletArc");Q0=makeQuery(id+"F2.boolean.opBoolean","SPLIT",FACE,{"disambiguationData":[TD([makeQuery(id+"F1.opExtrude","SWEPT_FACE",FACE,{"disambiguationData":[OSD([subQ6])]})])],"derivedFrom":makeQuery(id+"F1.opExtrude","CAP_FACE",FACE,{"disambiguationData":[OSD([subQ6,subQ8,subQ9,subQ7,subQ4,subQ3,subQ2,subQ1,subQ0,subQ5,subQ10,subQ11])],"isStart":true})});}
            var Q1;
            Q1=makeQuery(id+"F2.opExtrude","CAP_FACE",FACE,{"disambiguationData":[OSD([sQuery(id+"F0.wireOp",EDGE,"E12"),sQuery(id+"F0.wireOp",EDGE,"E13"),sQuery(id+"F0.wireOp",EDGE,"E14"),sQuery(id+"F0.wireOp",EDGE,"E15"),sQuery(id+"F0.wireOp",EDGE,"E17.filletArc"),sQuery(id+"F0.wireOp",EDGE,"E18.filletArc"),sQuery(id+"F0.wireOp",EDGE,"E19.filletArc"),sQuery(id+"F0.wireOp",EDGE,"E20.filletArc"),sQuery(id+"F0.wireOp",EDGE,"E25.0"),sQuery(id+"F0.wireOp",EDGE,"E25.1"),sQuery(id+"F0.wireOp",EDGE,"E25.2"),sQuery(id+"F0.wireOp",EDGE,"E25.3"),sQuery(id+"F0.wireOp",EDGE,"E25.4"),sQuery(id+"F0.wireOp",EDGE,"E25.5"),sQuery(id+"F0.wireOp",EDGE,"E25.6"),sQuery(id+"F0.wireOp",EDGE,"E25.7")])],"isStart":false});
            extrude(context, id + "F18", {"entities" : qUnion([Q0]), "endBound" : BoundingType.UP_TO_SURFACE, "depth" : 25.4 * mm, "endBoundEntityFace" : qUnion([Q1]), "offsetDistance" : 25.4 * mm});
        }
    });
